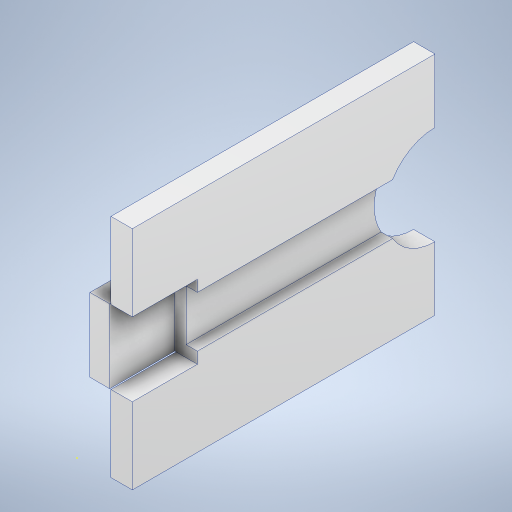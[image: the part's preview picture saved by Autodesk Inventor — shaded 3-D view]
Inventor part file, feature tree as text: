
AUTODESK INVENTOR PART (.ipt)
format: ipt  version: 2024 (Build 280153000, 153)  size: 321,536 bytes
history: native  units: mm
features: sketch x6, extrude x5
ambient origin geometry x8: Origin, YZ Plane, XZ Plane, XY Plane, X Axis, Y Axis, Z Axis, Center Point
bodies: Solid1 (feature_tree)
feature tree (11):
  extrude  "Extrusion1"  Depth=160.0mm TaperAngle=0.0deg
  extrude  "Extrusion2"  Depth=25.0mm
  extrude  "Extrusion4"  Depth=45.0mm
  extrude  "Extrusion5"  Depth=8.0mm
  sketch  "Sketch7"  dims[d10=36.0mm d11=80.0mm]
  extrude  "Extrusion6"  Depth=36.0mm
  sketch  "Sketch1"  dims[d0=550.0mm d1=160.0mm d2=0.0mm]
  sketch  "Sketch2"  dims[d4=25.0mm d5=25.0mm]
  sketch  "Sketch5"  dims[d6=0.0mm d7=45.0mm]
  sketch  "Sketch6"  dims[d8=45.0mm d9=8.0mm]
  sketch  "Sketch8"  dims[d12=80.0mm d13=150.0mm d14=0.0mm d15=30.0mm d28=39.130435mm d30=160.0mm d31=70.0mm d32=100.0mm d33=0.0mm d34=12.0mm d35=46.0mm d36=10.0mm d37=0.0mm d38=8.0mm d39=8.0mm d40=46.0mm d41=16.0mm d42=0.0mm]
